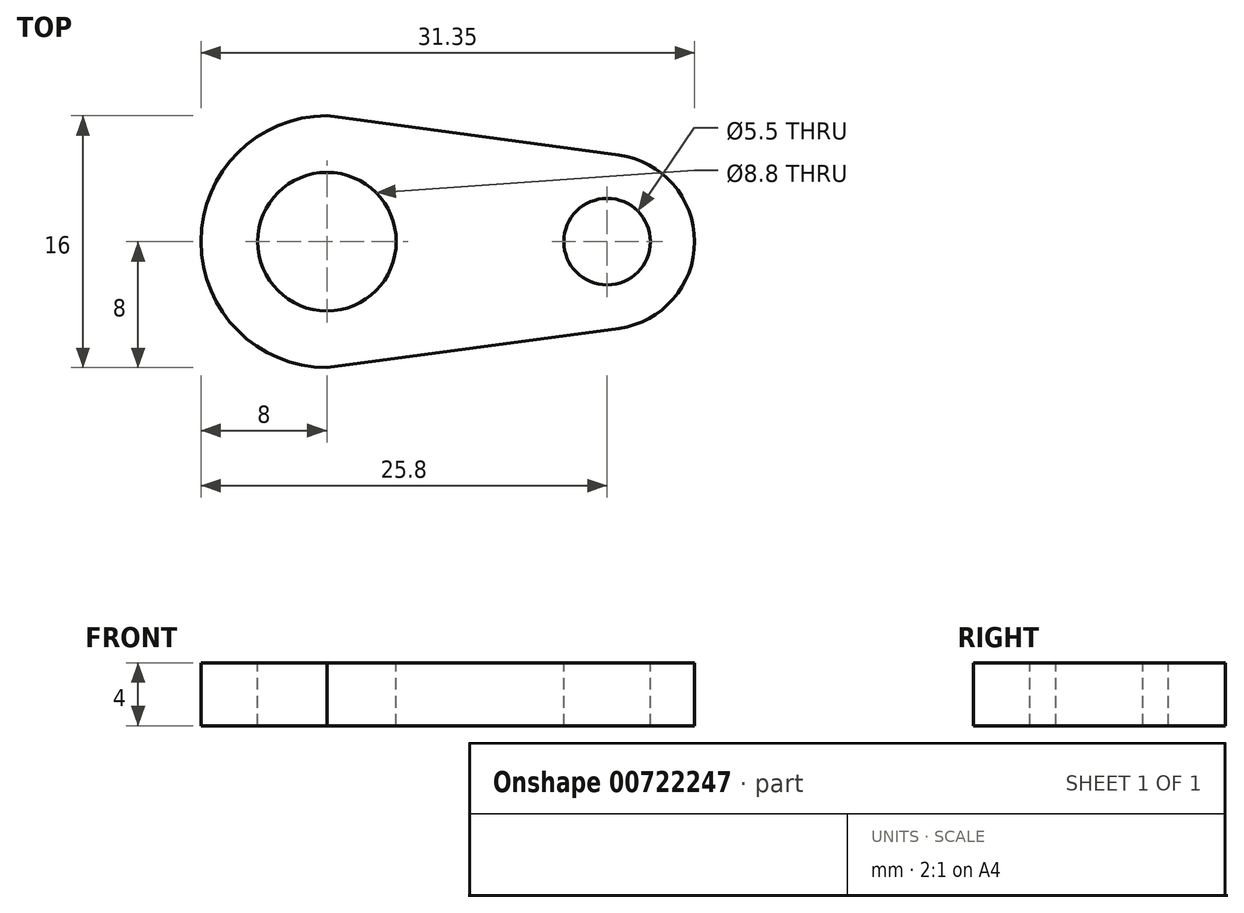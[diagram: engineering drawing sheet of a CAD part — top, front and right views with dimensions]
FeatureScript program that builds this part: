
annotation { "Feature Type Name" : "Feature", "Feature Type Description" : "" }
export const myFeature = defineFeature(function(context is Context, id is Id, definition is map)
    precondition{}
    {
        {
            var Q0;
            Q0=qCreatedBy(makeId("Top.planeOp"),FACE);
            var sketch = newSketch(context, id + "F0", { "sketchPlane" : qUnion([Q0])});
            skLineSegment(sketch, "E0", {"start": v(0, 0) * mm, "end": v(10, 0) * mm, "construction": true});
            skLineSegment(sketch, "E1", {"start": v(10, 0) * mm, "end": v(10, 16) * mm, "construction": true});
            skLineSegment(sketch, "E2", {"start": v(10, 8) * mm, "end": v(27.8, 8) * mm, "construction": true});
            skArc(sketch, "E3", {"start": v(12.12, 15.71) * mm, "mid": v(2, 8) * mm, "end": v(12.12, 0.29) * mm});
            skArc(sketch, "E4", {"start": v(28.54, 2.5) * mm, "mid": v(33.35, 8) * mm, "end": v(28.54, 13.5) * mm});
            skLineSegment(sketch, "E5", {"start": v(10, 0) * mm, "end": v(28.54, 2.5) * mm});
            skLineSegment(sketch, "E6", {"start": v(10, 16) * mm, "end": v(28.54, 13.5) * mm});
            skSolve(sketch);
        }
        {
            var Q0;
            {var subQ3=sQuery(id+"F0.wireOp",EDGE,"E4");Q0=makeQuery(id+"F0.imprint","IMPRINT",FACE,{"disambiguationData":[TD([[makeQuery(id+"F0.imprint","IMPRINT",EDGE,{"derivedFrom":subQ3}),1.0]])]});}
            var Q1;
            Q1=sQuery(id+"F0.wireOp",EDGE,"E2");
            extrude(context, id + "F1", {"entities" : qUnion([Q0]), "surfaceEntities" : qUnion([Q1]), "depth" : 4 * mm, "offsetDistance" : 25 * mm});
        }
        {
            var Q0;
            Q0=makeQuery(id+"F1.opExtrude","CAP_FACE",FACE,{"disambiguationData":[OSD([sQuery(id+"F0.wireOp",EDGE,"E3"),sQuery(id+"F0.wireOp",EDGE,"E4"),sQuery(id+"F0.wireOp",EDGE,"E5"),sQuery(id+"F0.wireOp",EDGE,"E6")])],"isStart":false});
            var sketch = newSketch(context, id + "F2", { "sketchPlane" : qUnion([Q0])});
            skCircle(sketch, "E7", {"center": v(10, 8) * mm, "radius": 4.4 * mm});
            skCircle(sketch, "E8", {"center": v(27.8, 8) * mm, "radius": 2.75 * mm});
            skLineSegment(sketch, "E9", {"start": v(10, 8) * mm, "end": v(27.8, 8) * mm, "construction": true});
            skSolve(sketch);
        }
        {
            var Q0;
            Q0=makeQuery(id+"F2.imprint","IMPRINT",FACE,{"disambiguationData":[TD([[makeQuery(id+"F2.imprint","IMPRINT",EDGE,{"derivedFrom":sQuery(id+"F2.wireOp",EDGE,"E7")}),1.0]])]});
            var Q1;
            Q1=makeQuery(id+"F2.imprint","IMPRINT",FACE,{"disambiguationData":[TD([[makeQuery(id+"F2.imprint","IMPRINT",EDGE,{"derivedFrom":sQuery(id+"F2.wireOp",EDGE,"E8")}),1.0]])]});
            var Q2;
            Q2=makeQuery(id+"F1.opExtrude","CAP_FACE",FACE,{"disambiguationData":[OSD([sQuery(id+"F0.wireOp",EDGE,"E3"),sQuery(id+"F0.wireOp",EDGE,"E4"),sQuery(id+"F0.wireOp",EDGE,"E5"),sQuery(id+"F0.wireOp",EDGE,"E6")])],"isStart":true});
            extrude(context, id + "F3", {"entities" : qUnion([Q0, Q1]), "operationType" : NewBodyOperationType.REMOVE, "endBound" : BoundingType.UP_TO_SURFACE, "oppositeDirection" : true, "depth" : 25 * mm, "endBoundEntityFace" : qUnion([Q2]), "offsetDistance" : 25 * mm});
        }
    });
